# Revit family: Lyra High Base modul
name_source: partatom
category: Furniture
units: mm (PartAtom-declared; Revit-internal decimal feet)

## family parameters
Always vertical = Yes
Cut with Voids When Loaded = No
OmniClass Number = 23.21.23.13.15
Room Calculation Point = No
Shared = No
Work Plane-Based = No

## types (2) — shared parameters
BIMobject category = PARK AND URBAN FURNITURE
Edition number = 1
IFC Classification = Furniture
Manufacturer = Hags
Manufacturer name = HAGS
OmniClass Code = 23-21 23 13 15
OmniClass Description = BICYCLE STORAGE
Product Guid = 90e49432-c870-4a59-897e-b15016e8f9bd
Product SKU = Cycle_Rack_Lyra_Detached
Product data url = https://www.hags.com
Product name = CYCLE RACK LYRA HIGH CAST IN PLACE BLACK BLACK
Product url = https://www.hags.com
QR code = https://www.hags.com
URL = https://www.hags.com
Uniclass 1.4 Code = L8211
Uniclass 1.4 Description = Furniture
zero-valued in all types: Default Elevation

## per-type parameters (varying)
| type | Body material | Body material_90 | Construction material | Model |
| 8090164 / Black | Hags - Steel - Powder coated - Black | Hags - Steel - Powder coated - Black | Hags - Steel - Powder coated - Black | 8090164 |
| 8090165 / Grey | Hags - Steel - Powder coated - Gray | Hags - Steel - Powder coated - Gray | Hags - Steel - Powder coated - Gray | 8037012 |

## geometry (parser evidence)
native form markers: Sweep x2
no freeform markers — native parametric forms only
